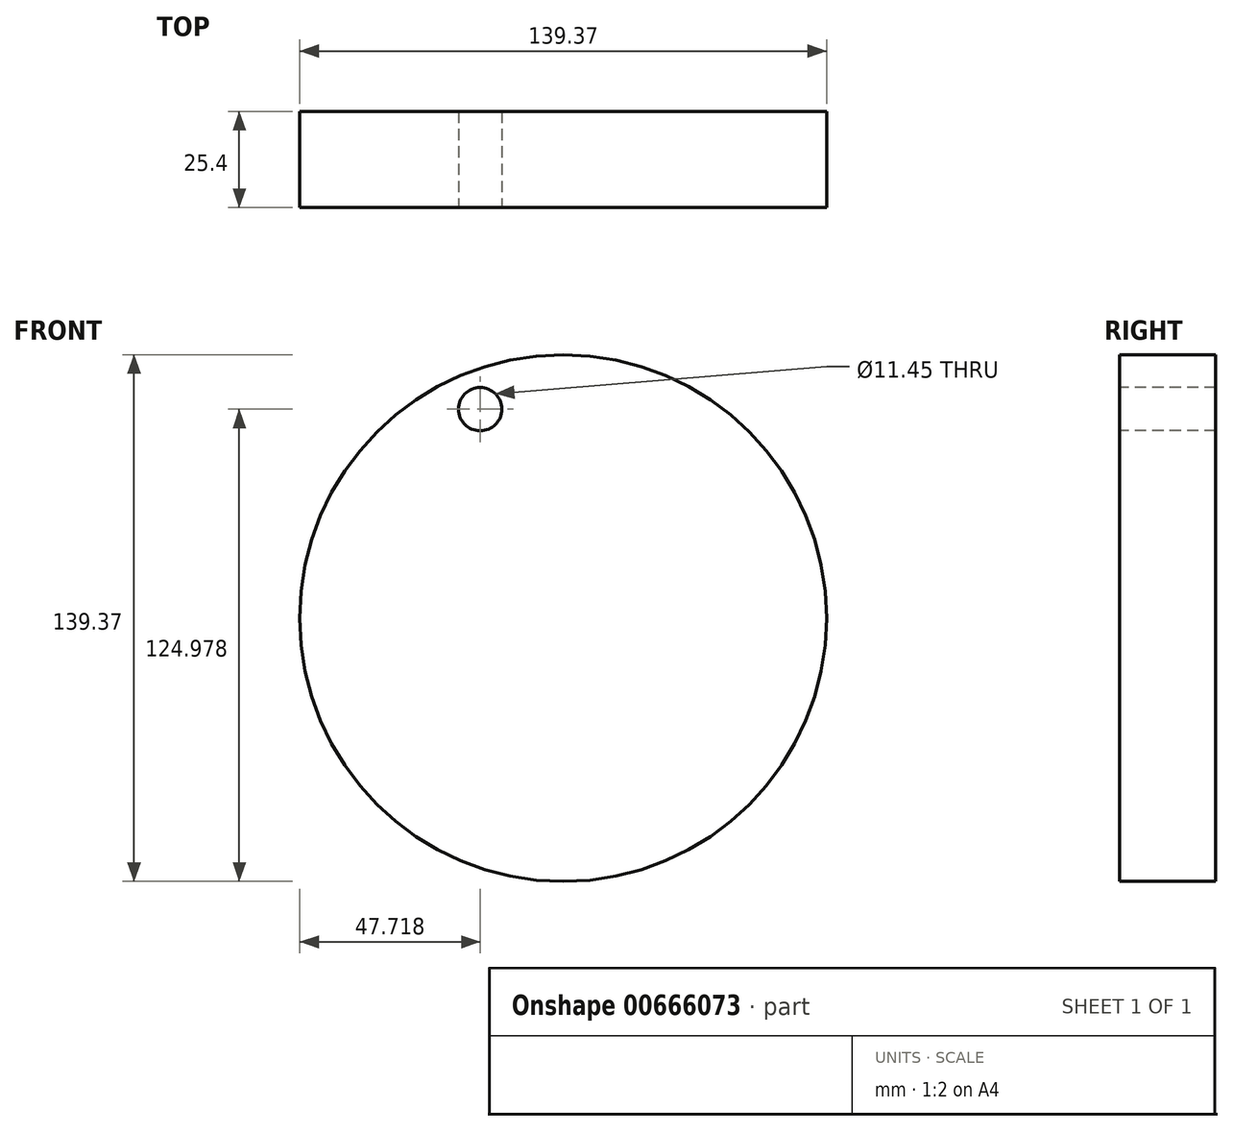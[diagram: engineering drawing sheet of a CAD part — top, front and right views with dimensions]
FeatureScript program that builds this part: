
annotation { "Feature Type Name" : "Feature", "Feature Type Description" : "" }
export const myFeature = defineFeature(function(context is Context, id is Id, definition is map)
    precondition{}
    {
        {
            var Q0;
            Q0=qCreatedBy(makeId("Front.planeOp"),FACE);
            var sketch = newSketch(context, id + "F0", { "sketchPlane" : qUnion([Q0])});
            skCircle(sketch, "E0", {"center": v(-61.97, 36.7) * mm, "radius": 69.68 * mm});
            skSolve(sketch);
        }
        {
            var Q0;
            Q0=makeQuery(id+"F0.imprint","IMPRINT",FACE,{"disambiguationData":[TD([[makeQuery(id+"F0.imprint","IMPRINT",EDGE,{"derivedFrom":sQuery(id+"F0.wireOp",EDGE,"E0")}),1.0]])]});
            extrude(context, id + "F1", {"entities" : qUnion([Q0]), "depth" : 25.4 * mm, "offsetDistance" : 25.4 * mm});
        }
        {
            var Q0;
            Q0=makeQuery(id+"F1.opExtrude","CAP_FACE",FACE,{"disambiguationData":[OSD([sQuery(id+"F0.wireOp",EDGE,"E0")])],"isStart":false});
            var sketch = newSketch(context, id + "F2", { "sketchPlane" : qUnion([Q0])});
            skCircle(sketch, "E1", {"center": v(-83.93, 91.99) * mm, "radius": 5.73 * mm});
            skSolve(sketch);
        }
        {
            var Q0;
            Q0 = qSketchRegion(id + "F2", true);
            extrude(context, id + "F3", {"entities" : qUnion([Q0]), "operationType" : NewBodyOperationType.REMOVE, "endBound" : BoundingType.THROUGH_ALL, "oppositeDirection" : true, "depth" : 25.4 * mm, "offsetDistance" : 25.4 * mm});
        }
    });
